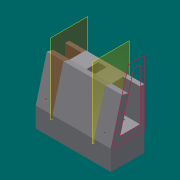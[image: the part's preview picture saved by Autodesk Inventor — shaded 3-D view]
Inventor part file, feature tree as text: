
AUTODESK INVENTOR PART (.ipt)
format: ipt  version: 2013 (Build 170138000, 138)  size: 201,216 bytes
history: native  units: mm
features: sketch x9, extrude x7, other x4, hole x2, mirror x1
ambient origin geometry x8: Origin, YZ Plane, XZ Plane, XY Plane, X Axis, Y Axis, Z Axis, Center Point
feature tree (23):
  other  "ソリッド1"
  extrude  "押し出し1"  Depth=80.0mm
  hole  "穴1"  [1 undecoded]
  other  "作業平面1"
  extrude  "押し出し4"  TaperAngle=15.0deg  [1 undecoded]
  mirror  "ミラー1"
  hole  "穴3"  [1 undecoded]
  sketch  "スケッチ7"
  other  "作業平面2"
  extrude  "押し出し5"  Depth=10.0mm
  other  "作業平面3"
  extrude  "押し出し6"  Depth=10.0mm
  extrude  "押し出し7"  Depth=10.0mm
  extrude  "押し出し8"  Depth=10.0mm
  extrude  "押し出し9"  Depth=10.0mm
  sketch  "スケッチ1"
  sketch  "スケッチ2"
  sketch  "スケッチ6"
  sketch  "スケッチ8"
  sketch  "スケッチ9"
  sketch  "スケッチ10"
  sketch  "スケッチ11"
  sketch  "スケッチ12"
note: 3 required parameter values undecoded (feature->parameter linkage not recoverable at this tier; creation-order binding heuristic only, values carry confidence <= 0.55)
